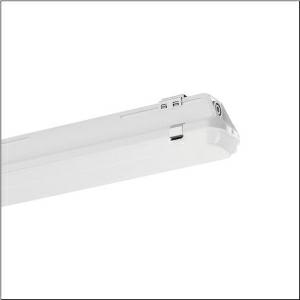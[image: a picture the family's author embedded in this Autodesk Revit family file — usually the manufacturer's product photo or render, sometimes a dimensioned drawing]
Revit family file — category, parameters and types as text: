
# Revit family: monsun_r__21_emergency_51fb107p487c3g_3320
name_source: partatom
category: Lighting Fixtures
units: mm (PartAtom-declared; Revit-internal decimal feet)

## family parameters
Cut with Voids When Loaded = No
Host = Face
Light Source = No
Part Type = Normal
Room Calculation Point = No
Round Connector Dimension = Use Diameter
Shared = No

## types (1)
- --- (1 x LED, 820 lm, 7.1 W, 4000K)
    Apparent Load = 7 VA
    CIE Flux Codes = 47 77 93 94 100
    Color Rendering = 80
    Color Temperature = 4000K
    Default Elevation = 1800 mm
    Description = Monsun® 21 emergency, damp-proof luminaire, chain hanger, primary optical cover: enclosure, of PMMA, light emission: direct distribution, primary light characteristic: symmetric, installation type: suspended mounting, surface-mounted, horizontal mounting, vertical mounting, LED, rated luminous flux: 8.090lm, luminous efficacy: 173lm/W, light colour: 840, colour temperature: 4000K, control gear: ON/OFF, with terminal, 4-pole, max. 2.5mm², mains connection: 220..240V, AC, 50/60Hz, rated input power: 51W, control gear: single battery element, battery: LiFePO4, 9Ah, housing, of glass-fibre reinforced polyester, uncoated, bright grey, incl. chain hanger, length: 1.590mm, width: 90mm, height: 88mm, clip for enclosure, of stainless steel (V2A), ceiling mounting element, of stainless steel (V2A), chain hanger, of stainless steel (V2A), protection rating (complete): IP66, insulation class (complete): insulation class I (protective earthing), certification: CE, UKCA, protection symbol: D, impact resistance: IK04, permissible operating ambient temperature: +5..+25°C, standard: EN 50419, EN 60598-2-1, EN 60598-2-22, corresponds to IFS (International Featured Standards) requirements for safety and quality in the food industry, for indoor or canopied outdoor use, no direct snow, no direct sun, no direct rain, LABS conformity tested according to VDMA 24364:2018-05, contact your sales advisor before using the luminaires in applications with unclear chemical exposure, large temperature fluctuations or condensation-forming humidity, packaging unit: 1 piece
    Height = 89 mm
    Lamp = 1 x LED
    Lamp Light Flux = 820 lm
    Lamp Power = 7.1 W
    Lamp count = 1
    Length = 1590 mm
    Luminous efficacy = 115 lm/W
    Manufacturer = Siteco
    ModVariant = No
    Model = 51FB107P487C3G
    Mounting Place = Ceiling
    Mounting Type = Surface mounted
    Number of Poles = 1
    OnlyDefault = Yes
    Power Factor = 1
    Product Name = Monsun® 21 emergency
    Product group = damp-proof luminaire
    ProductGroupID = 300
    Protection Class = Protection class I
    Protection Degree = IP 66
    RLX_Detail_Level = 1
    RLX_Emergency_Light_Flux = 0 lm
    RLX_Emergency_Type = 0
    RLX_Emergency_Type_DB = No
    RlxData = <blob elided: 88973 chars, md5=5d5429fc>
    Socket = socket
    Standby Power = 0 W
    System Light Flux = 820 lm
    System Power = 7 W
    Type Comments = : emergency light operation: 3 h
    Type Image = l_1319656.jpg
    URL = http://relux.com
    VarID = @adj_031766
    Voltage = 0 V
    Weight = 0.00 kg
    Width = 90 mm

## geometry (parser evidence)
native form markers: Blend x4, Sweep x14
no freeform markers — native parametric forms only
